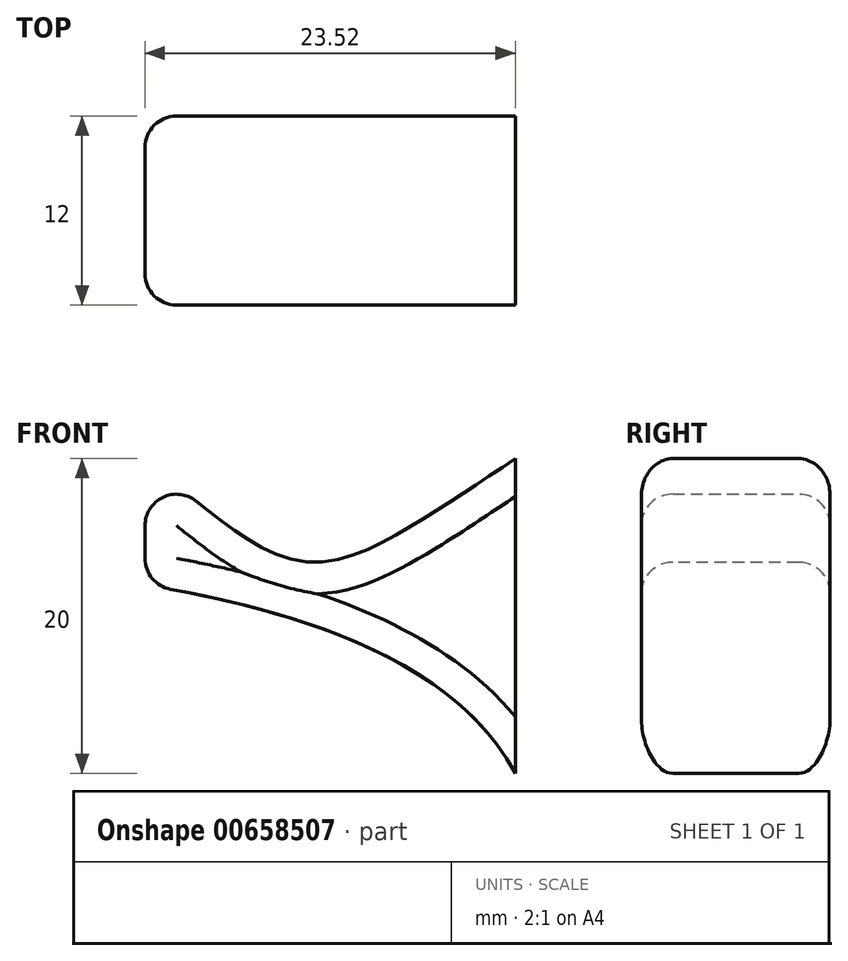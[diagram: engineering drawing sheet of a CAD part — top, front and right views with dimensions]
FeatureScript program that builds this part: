
annotation { "Feature Type Name" : "Feature", "Feature Type Description" : "" }
export const myFeature = defineFeature(function(context is Context, id is Id, definition is map)
    precondition{}
    {
        {
            var Q0;
            Q0=qCreatedBy(makeId("Front.planeOp"),FACE);
            var sketch = newSketch(context, id + "F0", { "sketchPlane" : qUnion([Q0])});
            skLineSegment(sketch, "E0", {"start": v(13.08, 0) * mm, "end": v(13.08, -20) * mm});
            skFitSpline(sketch, "E1", {"points": [v(13.08, -20) * mm, v(-10.44, -8) * mm], "startDerivative": vector(-13.48, 25.19) * mm, "endDerivative": vector(-19.87, 3.62) * mm});
            skLineSegment(sketch, "E2", {"start": v(-10.44, -8) * mm, "end": v(-10.44, 0) * mm});
            skFitSpline(sketch, "E3", {"points": [v(-10.44, 0) * mm, v(13.08, 0) * mm], "startDerivative": vector(31.31, -26.36) * mm, "endDerivative": vector(39.25, 26.36) * mm});
            skSolve(sketch);
        }
        {
            var Q0;
            Q0=makeQuery(id+"F0.imprint","IMPRINT",FACE,{"disambiguationData":[TD([[makeQuery(id+"F0.imprint","IMPRINT",EDGE,{"derivedFrom":sQuery(id+"F0.wireOp",EDGE,"E0")}),-1.0]])]});
            extrude(context, id + "F1", {"entities" : qUnion([Q0]), "depth" : 12 * mm, "offsetDistance" : 25 * mm});
        }
        {
            var Q0;
            Q0=makeQuery(id+"F1.opExtrude","SWEPT_EDGE",EDGE,{"disambiguationData":[OSD([sQuery(id+"F0.wireOp",EDGE,"E2"),sQuery(id+"F0.wireOp",EDGE,"E3")])]});
            var Q1;
            Q1=makeQuery(id+"F1.opExtrude","SWEPT_EDGE",EDGE,{"disambiguationData":[OSD([sQuery(id+"F0.wireOp",EDGE,"E1"),sQuery(id+"F0.wireOp",EDGE,"E2")])]});
            var Q2;
            Q2=makeQuery(id+"F1.opExtrude","CAP_EDGE",EDGE,{"disambiguationData":[OSD([sQuery(id+"F0.wireOp",EDGE,"E3")])],"isStart":false});
            var Q3;
            Q3=makeQuery(id+"F1.opExtrude","CAP_EDGE",EDGE,{"disambiguationData":[OSD([sQuery(id+"F0.wireOp",EDGE,"E3")])],"isStart":true});
            var Q4;
            Q4=makeQuery(id+"F1.opExtrude","CAP_EDGE",EDGE,{"disambiguationData":[OSD([sQuery(id+"F0.wireOp",EDGE,"E1")])],"isStart":false});
            var Q5;
            Q5=makeQuery(id+"F1.opExtrude","CAP_EDGE",EDGE,{"disambiguationData":[OSD([sQuery(id+"F0.wireOp",EDGE,"E1")])],"isStart":true});
            var Q6;
            Q6=makeQuery(id+"F1.opExtrude","CAP_EDGE",EDGE,{"disambiguationData":[OSD([sQuery(id+"F0.wireOp",EDGE,"E2")])],"isStart":true});
            var Q7;
            Q7=makeQuery(id+"F1.opExtrude","CAP_EDGE",EDGE,{"disambiguationData":[OSD([sQuery(id+"F0.wireOp",EDGE,"E2")])],"isStart":false});
            fillet(context, id + "F2", {"entities" : qUnion([Q0, Q1, Q2, Q3, Q4, Q5, Q6, Q7]), "radius" : 2 * mm, "tangentPropagation" : true, "allowEdgeOverflow" : false});
        }
    });
